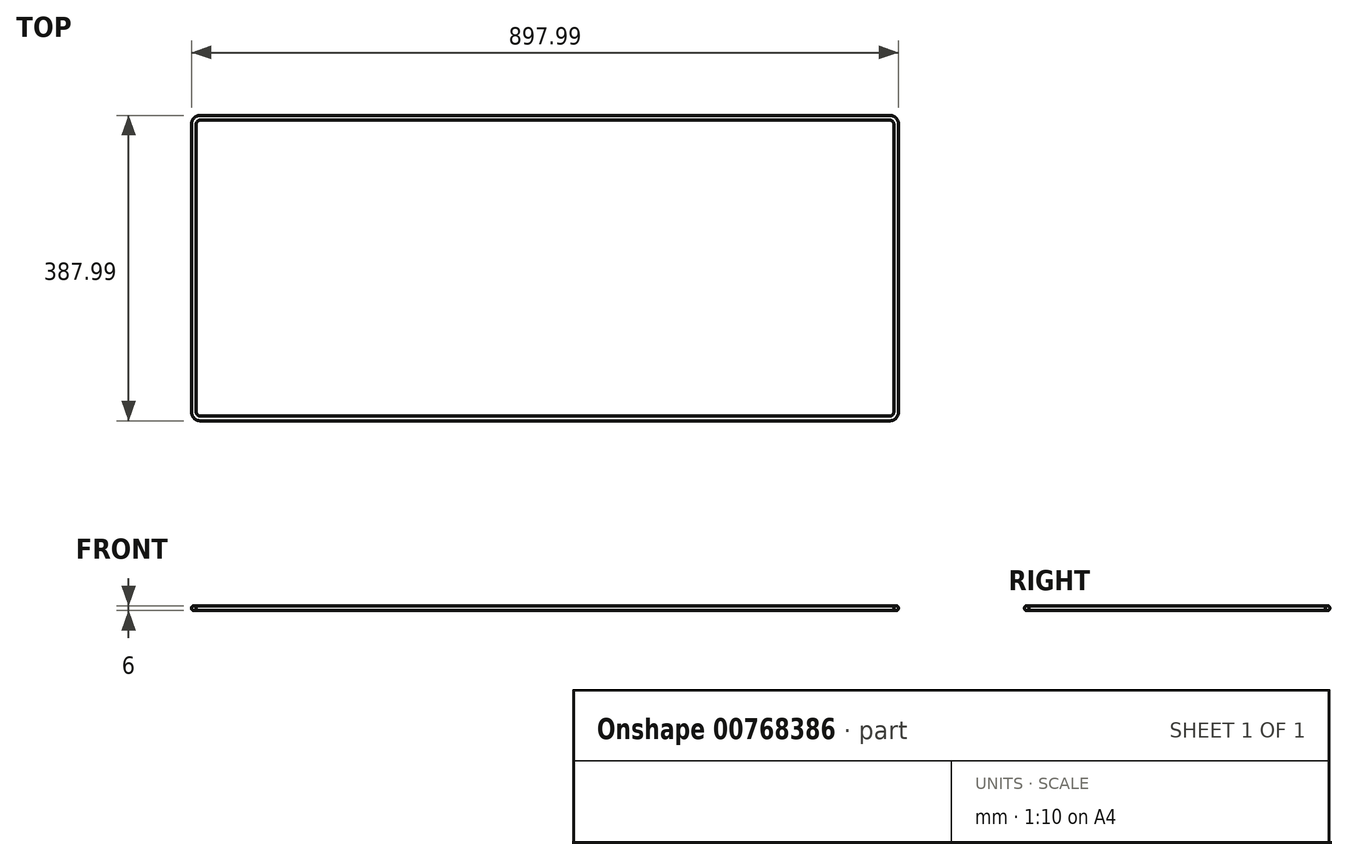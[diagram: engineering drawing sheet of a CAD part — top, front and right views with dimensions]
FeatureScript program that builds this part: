
annotation { "Feature Type Name" : "Feature", "Feature Type Description" : "" }
export const myFeature = defineFeature(function(context is Context, id is Id, definition is map)
    precondition{}
    {
        {
            var Q0;
            Q0=qCreatedBy(makeId("Top.planeOp"),FACE);
            var sketch = newSketch(context, id + "F0", { "sketchPlane" : qUnion([Q0])});
            skLineSegment(sketch, "E0.bottom", {"start": v(-353.23, 205.76) * mm, "end": v(522.77, 205.76) * mm});
            skLineSegment(sketch, "E0.top", {"start": v(-353.23, -184.24) * mm, "end": v(522.77, -184.24) * mm});
            skLineSegment(sketch, "E0.left", {"start": v(-365.23, 193.76) * mm, "end": v(-365.23, -172.24) * mm});
            skLineSegment(sketch, "E0.right", {"start": v(534.77, 193.76) * mm, "end": v(534.77, -172.24) * mm});
            skPoint(sketch, "E1.visualSharp", {"position": v(-365.23, -184.24) * mm});
            skArc(sketch, "E1.filletArc", {"start": v(-365.23, -172.24) * mm, "mid": v(-361.72, -180.73) * mm, "end": v(-353.23, -184.24) * mm});
            skPoint(sketch, "E2.visualSharp", {"position": v(-365.23, 205.76) * mm});
            skArc(sketch, "E2.filletArc", {"start": v(-353.23, 205.76) * mm, "mid": v(-361.72, 202.24) * mm, "end": v(-365.23, 193.76) * mm});
            skPoint(sketch, "E3.visualSharp", {"position": v(534.77, -184.24) * mm});
            skArc(sketch, "E3.filletArc", {"start": v(522.77, -184.24) * mm, "mid": v(531.25, -180.73) * mm, "end": v(534.77, -172.24) * mm});
            skPoint(sketch, "E4.visualSharp", {"position": v(534.77, 205.76) * mm});
            skArc(sketch, "E4.filletArc", {"start": v(534.77, 193.76) * mm, "mid": v(531.25, 202.24) * mm, "end": v(522.77, 205.76) * mm});
            skSolve(sketch);
        }
        {
            var Q0;
            Q0=qCreatedBy(makeId("Front.planeOp"),FACE);
            var sketch = newSketch(context, id + "F1", { "sketchPlane" : qUnion([Q0])});
            skCircle(sketch, "E5", {"center": v(-361.23, -20.36) * mm, "radius": 3 * mm});
            skSolve(sketch);
        }
        {
            var Q0;
            Q0=makeQuery(id+"F1.imprint","IMPRINT",FACE,{"disambiguationData":[TD([[makeQuery(id+"F1.imprint","IMPRINT",EDGE,{"derivedFrom":sQuery(id+"F1.wireOp",EDGE,"E5")}),1.0]])]});
            var Q1;
            Q1=sQuery(id+"F0.wireOp",EDGE,"E0.left");
            var Q2;
            Q2=sQuery(id+"F0.wireOp",EDGE,"E1.filletArc");
            var Q3;
            Q3=sQuery(id+"F0.wireOp",EDGE,"E0.top");
            var Q4;
            Q4=sQuery(id+"F0.wireOp",EDGE,"E2.filletArc");
            var Q5;
            Q5=sQuery(id+"F0.wireOp",EDGE,"E0.bottom");
            var Q6;
            Q6=sQuery(id+"F0.wireOp",EDGE,"E3.filletArc");
            var Q7;
            Q7=sQuery(id+"F0.wireOp",EDGE,"E0.right");
            var Q8;
            Q8=sQuery(id+"F0.wireOp",EDGE,"E4.filletArc");
            sweep(context, id + "F2", {"profiles" : qUnion([Q0]), "path" : qUnion([Q1, Q2, Q3, Q4, Q5, Q6, Q7, Q8])});
        }
    });
